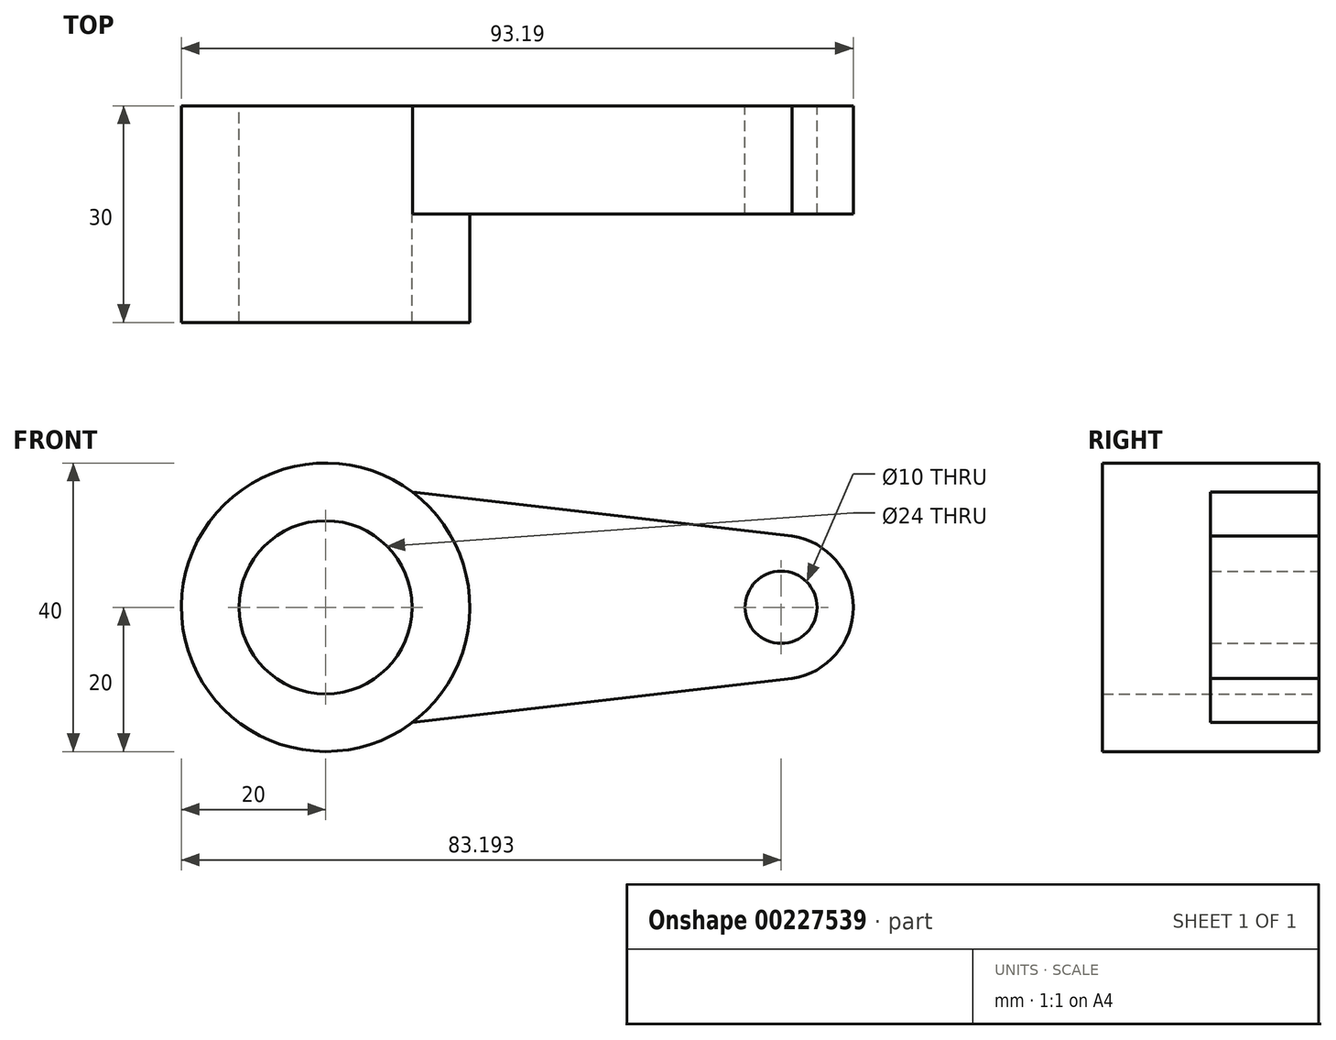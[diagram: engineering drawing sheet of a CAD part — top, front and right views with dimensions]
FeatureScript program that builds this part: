
annotation { "Feature Type Name" : "Feature", "Feature Type Description" : "" }
export const myFeature = defineFeature(function(context is Context, id is Id, definition is map)
    precondition{}
    {
        {
            var Q0;
            Q0=qCreatedBy(makeId("Front.planeOp"),FACE);
            var sketch = newSketch(context, id + "F0", { "sketchPlane" : qUnion([Q0])});
            skCircle(sketch, "E0", {"center": v(0, 0) * mm, "radius": 20 * mm});
            skArc(sketch, "E1", {"start": v(64.74, -9.88) * mm, "mid": v(73.2, 0) * mm, "end": v(64.74, 9.88) * mm});
            skCircle(sketch, "E2", {"center": v(0, 0) * mm, "radius": 12 * mm});
            skCircle(sketch, "E3", {"center": v(63.2, 0) * mm, "radius": 5 * mm});
            skLineSegment(sketch, "E4", {"start": v(64.74, 9.88) * mm, "end": v(12.04, 15.97) * mm});
            skLineSegment(sketch, "E5.MirrorCS", {"start": v(64.74, -9.88) * mm, "end": v(12.04, -15.97) * mm});
            skSolve(sketch);
        }
        {
            var Q0;
            Q0=makeQuery(id+"F0.imprint","IMPRINT",FACE,{"disambiguationData":[TD([[makeQuery(id+"F0.imprint","IMPRINT",EDGE,{"derivedFrom":sQuery(id+"F0.wireOp",EDGE,"E1")}),1.0]])]});
            extrude(context, id + "F1", {"entities" : qUnion([Q0]), "depth" : 15 * mm});
        }
        {
            var Q0;
            Q0=makeQuery(id+"F0.imprint","IMPRINT",FACE,{"disambiguationData":[TD([[makeQuery(id+"F0.imprint","IMPRINT",EDGE,{"derivedFrom":sQuery(id+"F0.wireOp",EDGE,"E2")}),-1.0]])]});
            extrude(context, id + "F2", {"entities" : qUnion([Q0]), "operationType" : NewBodyOperationType.ADD, "depth" : 30 * mm});
        }
    });
